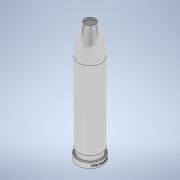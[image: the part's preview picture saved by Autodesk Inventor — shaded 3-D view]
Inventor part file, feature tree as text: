
AUTODESK INVENTOR PART (.ipt)
format: ipt  version: 2021 (Build 250183000, 183)  size: 603,648 bytes
history: native  units: mm
features: sketch x9, extrude x7, other x5
ambient origin geometry x8: Origin, YZ Plane, XZ Plane, XY Plane, X Axis, Y Axis, Z Axis, Center Point
bodies: Body1 (feature_tree)
feature tree (21):
  other  "Sólido1"
  extrude  "Extrusão1"  Depth=1.5mm TaperAngle=0.0deg
  extrude  "Extrusão2"  Depth=1.5mm TaperAngle=0.0deg
  extrude  "Extrusão3"  Depth=22.0mm TaperAngle=0.0deg
  other  "Revolução2"
  other  "Plano de trabalho1"
  extrude  "Extrusão4"  Depth=36.963mm
  extrude  "Extrusão5"  Depth=3.963mm TaperAngle=0.0deg
  extrude  "Extrusão6"  Depth=2.5mm TaperAngle=0.0deg
  extrude  "Extrusão7"  Depth=0.5mm TaperAngle=0.0deg
  other  "Plano de trabalho2"
  other  "Relevo1"
  sketch  "Esboço1"  dims[d0=7.0mm d1=1.5mm d2=0.0mm]
  sketch  "Esboço2"  dims[d3=6.0mm d4=1.5mm d5=0.0mm]
  sketch  "Esboço3"  dims[d6=6.5mm d7=22.0mm d8=0.0mm]
  sketch  "Esboço4"  dims[d10=90.0deg d11=36.963mm]
  sketch  "Esboço5"  dims[d12=3.0mm d13=3.963mm d14=0.0mm]
  sketch  "Esboço6"  dims[d15=2.5mm d16=0.5mm d17=0.0mm]
  sketch  "Esboço7"  dims[d18=2.4mm d19=0.5mm d20=0.0mm]
  sketch  "Esboço8"  dims[d21=0.1mm]
  sketch  "Esboço10"  dims[d22=0.5mm d23=0.0mm d24=3.5mm d25=1.0mm d26=0.0mm]
